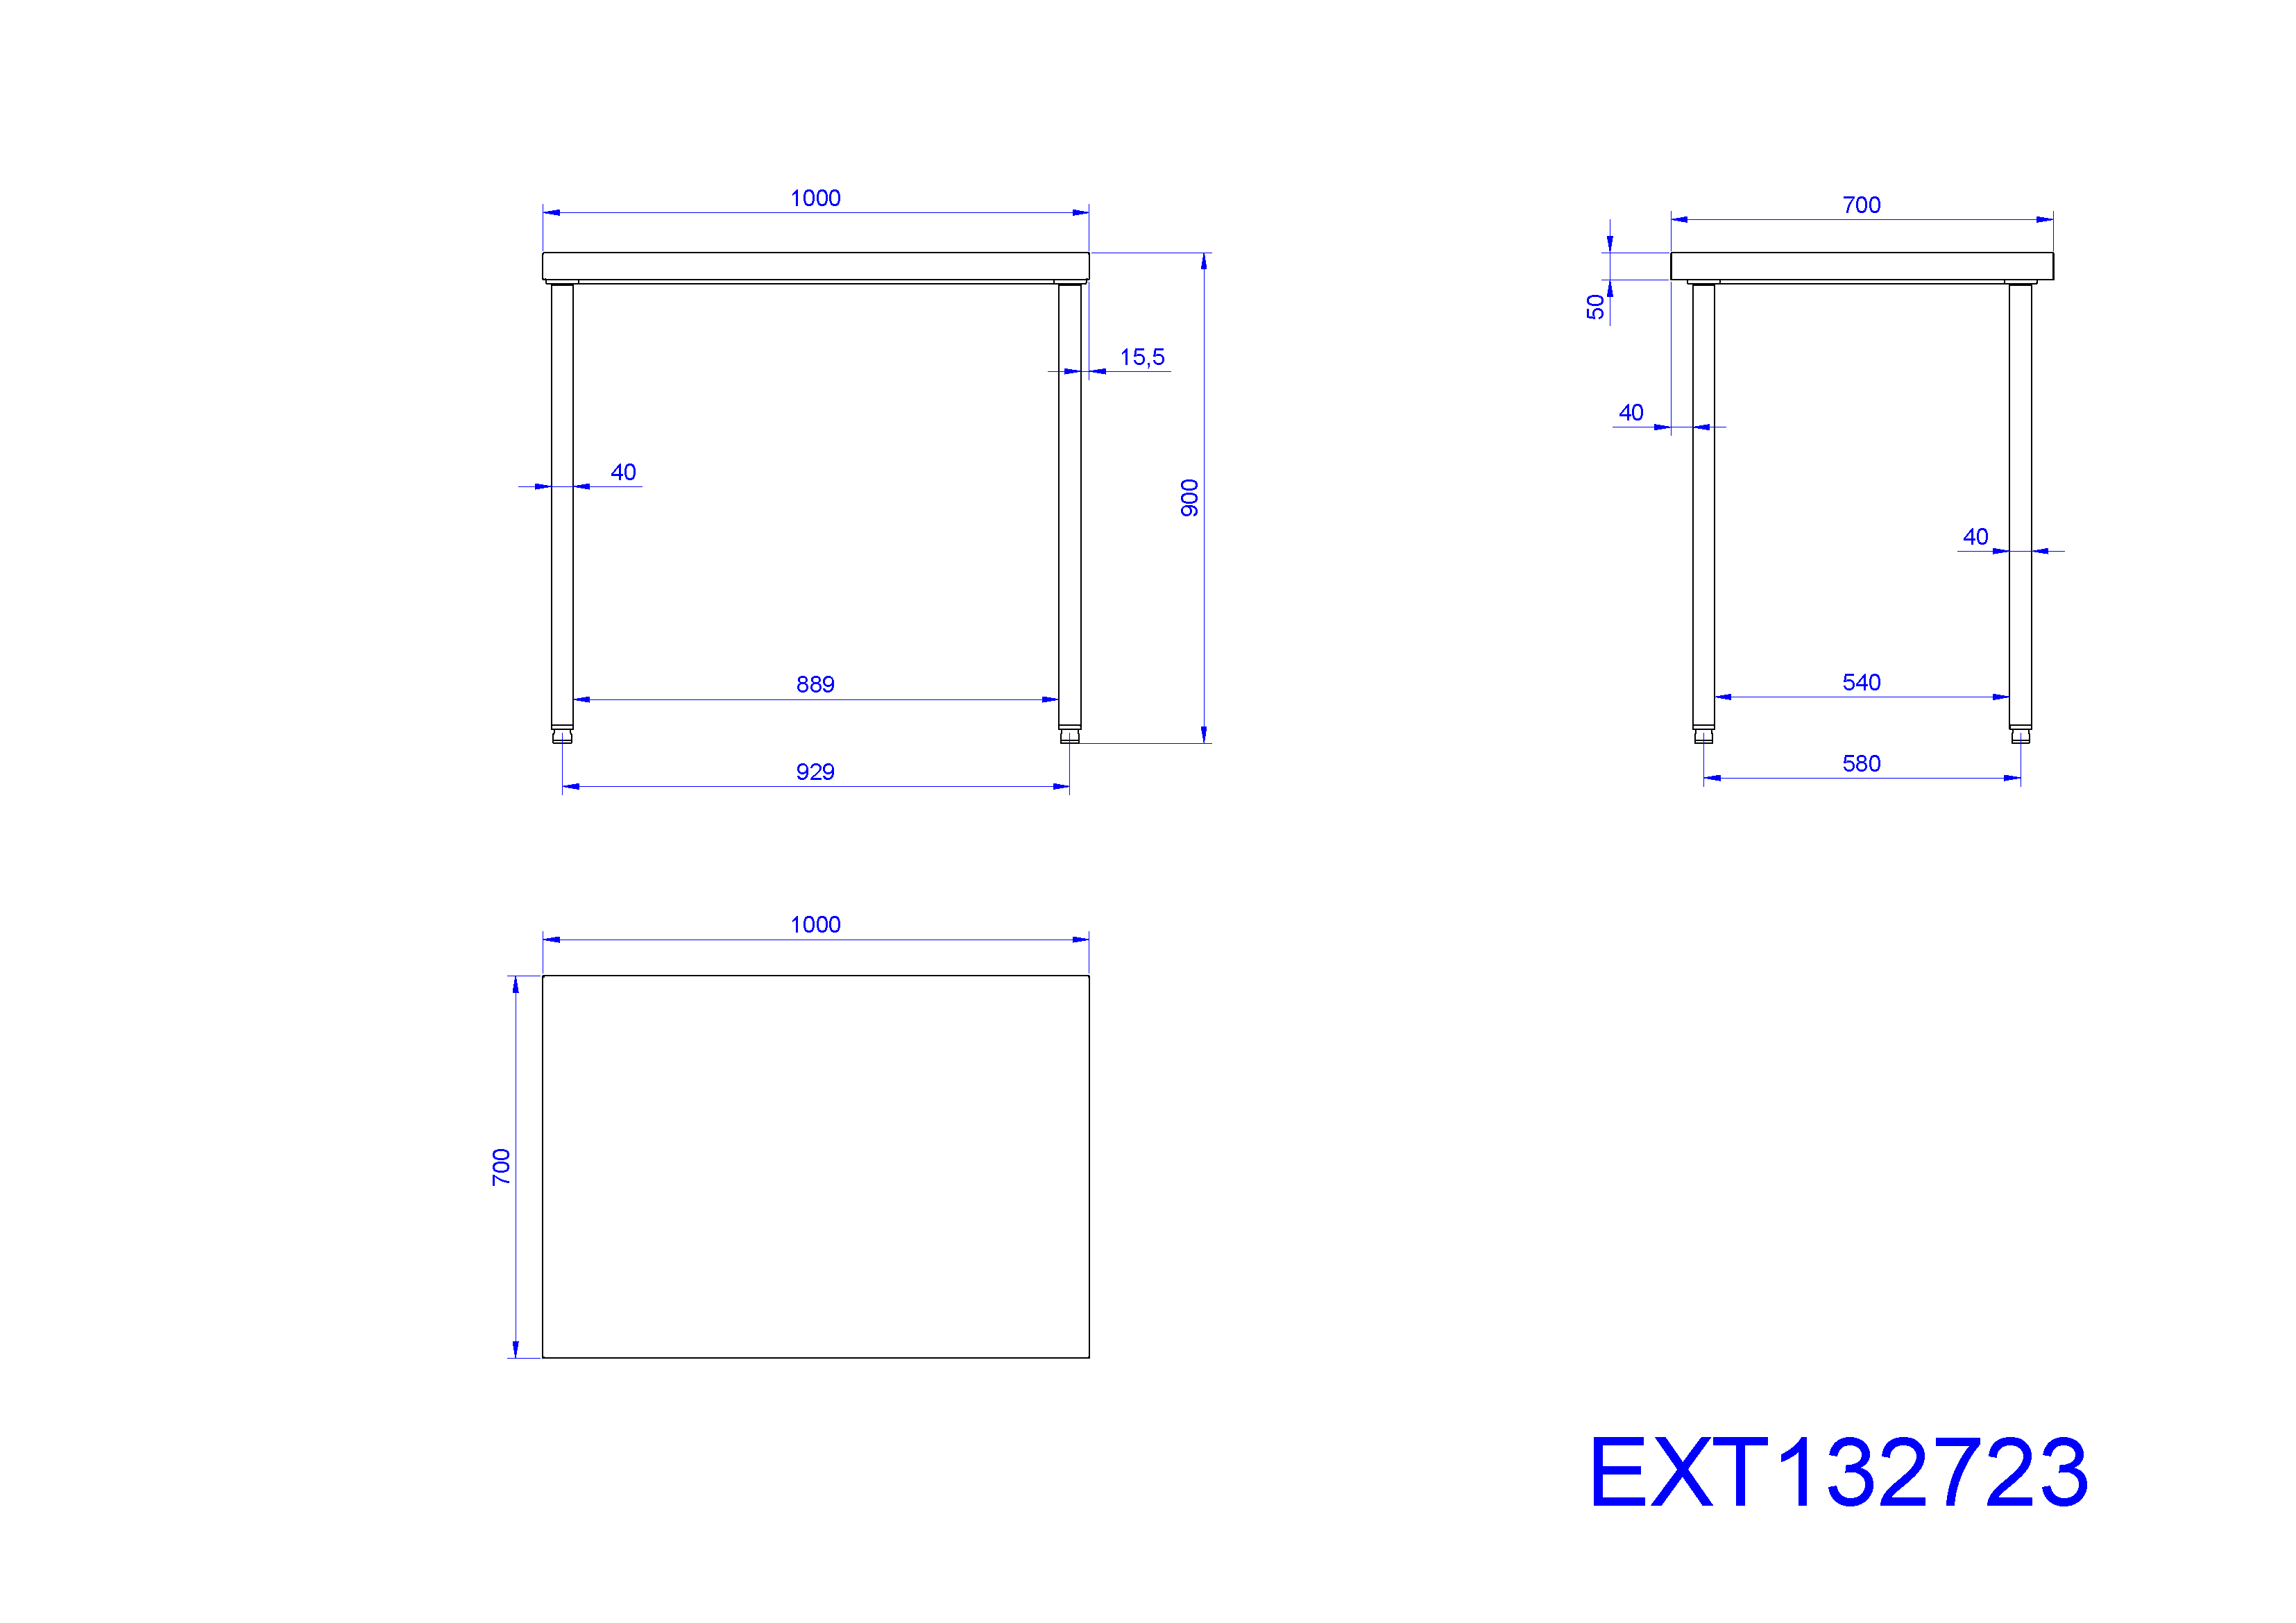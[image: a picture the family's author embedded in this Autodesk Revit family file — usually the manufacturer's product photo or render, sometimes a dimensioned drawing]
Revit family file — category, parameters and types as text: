
# Revit family: QF_ELECTROLUXPROFESSIONAL_132843_WTD1807N
name_source: partatom
category: Attrezzature speciali
units: mm (PartAtom-declared; Revit-internal decimal feet)

## family parameters
Basato su piano di lavoro = No
Condiviso = No
Punto di calcolo locali = No
Quota connettore circolare = Usa diametro
Sempre verticale = Sì
Taglio con vuoti quando caricato = No
Tipo di parte = Normale

## types (1)
- Standard
    Accessory = Sì
    Cold Water Size = 0 mm
    Compressed Air Pressure = 0.0 Pa
    Compressed Air Size = 0 mm
    Compressed Air Volume = 0.0 L/s
    Condensate Return Size = 0 mm
    Cycle = 0 Hz
    Depth Actual = 700 mm  [stored 2.29659 ft]
    Descrizione = WORK TABLE-DISASSEMBLED 1800MM
    Direct Waste Size = 0 mm
    Gas Input Pressure = 0
    Gas KW = 0
    Gas Size = 0 mm
    HP = 0 HP
    Height Actual = 900 mm  [stored 2.95276 ft]
    Hot Water Size = 0 mm
    Item Number = 132843
    Length Actual = 1800 mm  [stored 5.90551 ft]
    Modello = WTD1807N
    Phase = 0
    Produttore = Electrolux Professional
    Prospetto di default = 0 mm  [stored 0 ft]
    Refrigerant Compressor Remote = Sì
    Refrigeration Liquid Line Size = 0 mm  [stored 0 ft]
    Refrigeration Suction Line Size = 0 mm  [stored 0 ft]
    Steam Consumption per Hour = 0
    Steam Supply Maximum Pressure = 0.0 Pa
    Steam Supply Minimum Pressure = 0.0 Pa
    Steam Supply Size = 0 mm
    URL = https://www.electroluxprofessional.com
    URL Manufacturer = https://www.electroluxprofessional.com
    Volts = 0 V
    Watts = 0 W
    Weight = 57.00 kg

note: source unit labels omitted for Gas Input Pressure — the stored unit's dimension contradicts the parameter name (converter mislabeling)

note: [stored X ft] marks values corroborated as IEEE doubles in the binary element streams (Revit-internal decimal feet)

## geometry (parser evidence)
native form markers: Sweep x2
no freeform markers — native parametric forms only
